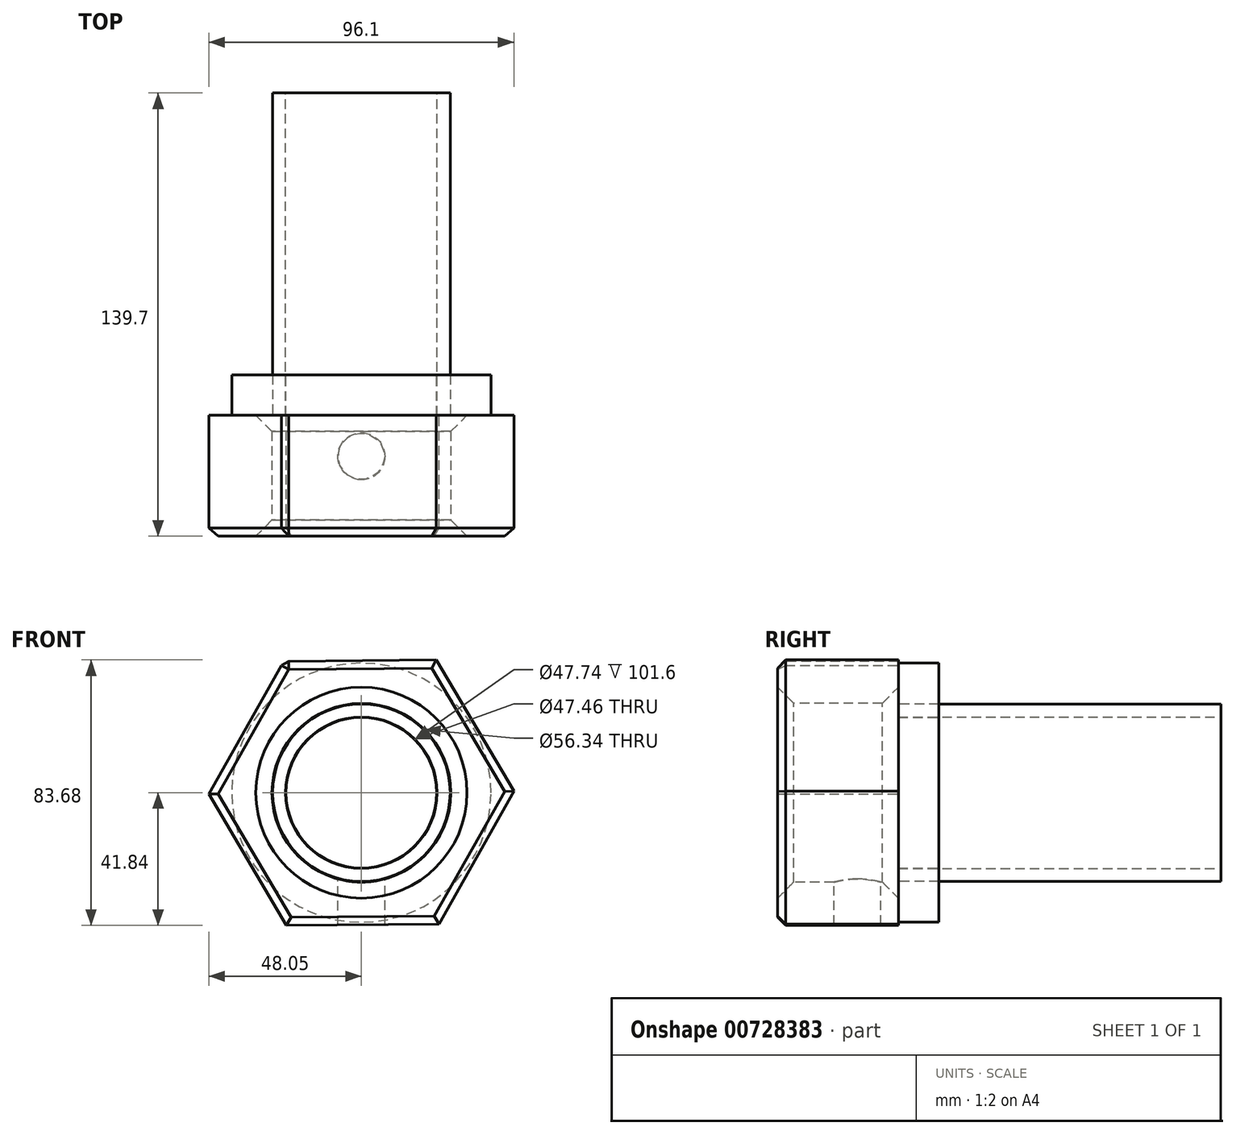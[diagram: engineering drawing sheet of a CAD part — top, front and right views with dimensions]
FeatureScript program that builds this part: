
annotation { "Feature Type Name" : "Feature", "Feature Type Description" : "" }
export const myFeature = defineFeature(function(context is Context, id is Id, definition is map)
    precondition{}
    {
        {
            var Q0;
            Q0=qCreatedBy(makeId("Front.planeOp"),FACE);
            var sketch = newSketch(context, id + "F0", { "sketchPlane" : qUnion([Q0])});
            skCircle(sketch, "E0.cCircle", {"center": v(0, 0) * mm, "radius": 41.62 * mm, "construction": true});
            skLineSegment(sketch, "E0.0", {"start": v(23.64, 41.84) * mm, "end": v(48.05, 0.45) * mm});
            skLineSegment(sketch, "E0.1", {"start": v(48.05, 0.45) * mm, "end": v(24.42, -41.4) * mm});
            skLineSegment(sketch, "E0.2", {"start": v(24.42, -41.4) * mm, "end": v(-23.64, -41.84) * mm});
            skLineSegment(sketch, "E0.3", {"start": v(-23.64, -41.84) * mm, "end": v(-48.05, -0.45) * mm});
            skLineSegment(sketch, "E0.4", {"start": v(-48.05, -0.45) * mm, "end": v(-24.42, 41.4) * mm});
            skLineSegment(sketch, "E0.5", {"start": v(-24.42, 41.4) * mm, "end": v(23.64, 41.84) * mm});
            skPoint(sketch, "E0.0.midPoint", {"position": v(35.85, 21.15) * mm});
            skSolve(sketch);
        }
        {
            var Q0;
            Q0 = qSketchRegion(id + "F0", true);
            extrude(context, id + "F1", {"entities" : qUnion([Q0]), "depth" : 38.1 * mm, "offsetDistance" : 25.4 * mm});
        }
        {
            var Q0;
            Q0=makeQuery(id+"F1.opExtrude","CAP_FACE",FACE,{"disambiguationData":[OSD([sQuery(id+"F0.wireOp",EDGE,"E0.0"),sQuery(id+"F0.wireOp",EDGE,"E0.1"),sQuery(id+"F0.wireOp",EDGE,"E0.2"),sQuery(id+"F0.wireOp",EDGE,"E0.3"),sQuery(id+"F0.wireOp",EDGE,"E0.4"),sQuery(id+"F0.wireOp",EDGE,"E0.5")])],"isStart":false});
            var sketch = newSketch(context, id + "F2", { "sketchPlane" : qUnion([Q0])});
            skCircle(sketch, "E1", {"center": v(0, 0) * mm, "radius": 29.53 * mm});
            skSolve(sketch);
        }
        {
            var Q0;
            Q0=makeQuery(id+"F2.imprint","IMPRINT",FACE,{"disambiguationData":[TD([[makeQuery(id+"F2.imprint","IMPRINT",EDGE,{"derivedFrom":sQuery(id+"F2.wireOp",EDGE,"E1")}),1.0]])]});
            extrude(context, id + "F3", {"entities" : qUnion([Q0]), "operationType" : NewBodyOperationType.REMOVE, "depth" : 38.1 * mm, "offsetDistance" : 25.4 * mm});
        }
        {
            var Q0;
            Q0=makeQuery(id+"F1.opExtrude","CAP_FACE",FACE,{"disambiguationData":[OSD([sQuery(id+"F0.wireOp",EDGE,"E0.0"),sQuery(id+"F0.wireOp",EDGE,"E0.1"),sQuery(id+"F0.wireOp",EDGE,"E0.2"),sQuery(id+"F0.wireOp",EDGE,"E0.3"),sQuery(id+"F0.wireOp",EDGE,"E0.4"),sQuery(id+"F0.wireOp",EDGE,"E0.5")])],"isStart":false});
            var sketch = newSketch(context, id + "F4", { "sketchPlane" : qUnion([Q0])});
            skCircle(sketch, "E2", {"center": v(0, 0) * mm, "radius": 28.17 * mm});
            skSolve(sketch);
        }
        {
            var Q0;
            Q0 = qSketchRegion(id + "F4", true);
            extrude(context, id + "F5", {"entities" : qUnion([Q0]), "operationType" : NewBodyOperationType.REMOVE, "oppositeDirection" : true, "depth" : 38.1 * mm, "offsetDistance" : 25.4 * mm});
        }
        {
            var Q0;
            Q0=makeQuery(id+"F1.opExtrude","CAP_FACE",FACE,{"disambiguationData":[OSD([sQuery(id+"F0.wireOp",EDGE,"E0.0"),sQuery(id+"F0.wireOp",EDGE,"E0.1"),sQuery(id+"F0.wireOp",EDGE,"E0.2"),sQuery(id+"F0.wireOp",EDGE,"E0.3"),sQuery(id+"F0.wireOp",EDGE,"E0.4"),sQuery(id+"F0.wireOp",EDGE,"E0.5")])],"isStart":false});
            var sketch = newSketch(context, id + "F6", { "sketchPlane" : qUnion([Q0])});
            skSolve(sketch);
        }
        {
            var Q0;
            Q0=makeQuery(id+"F1.opExtrude","CAP_EDGE",EDGE,{"disambiguationData":[OSD([sQuery(id+"F0.wireOp",EDGE,"E0.3")])],"isStart":false});
            chamfer(context, id + "F7", {"entities" : qUnion([Q0]), "width" : 2.54 * mm, "tangentPropagation" : true});
        }
        {
            var Q0;
            Q0=makeQuery(id+"F1.opExtrude","CAP_EDGE",EDGE,{"disambiguationData":[OSD([sQuery(id+"F0.wireOp",EDGE,"E0.5")])],"isStart":false});
            var Q1;
            Q1=makeQuery(id+"F1.opExtrude","CAP_EDGE",EDGE,{"disambiguationData":[OSD([sQuery(id+"F0.wireOp",EDGE,"E0.0")])],"isStart":false});
            var Q2;
            Q2=makeQuery(id+"F1.opExtrude","CAP_EDGE",EDGE,{"disambiguationData":[OSD([sQuery(id+"F0.wireOp",EDGE,"E0.1")])],"isStart":false});
            var Q3;
            Q3=makeQuery(id+"F1.opExtrude","CAP_EDGE",EDGE,{"disambiguationData":[OSD([sQuery(id+"F0.wireOp",EDGE,"E0.2")])],"isStart":false});
            var Q4;
            Q4=makeQuery(id+"F1.opExtrude","CAP_EDGE",EDGE,{"disambiguationData":[OSD([sQuery(id+"F0.wireOp",EDGE,"E0.4")])],"isStart":false});
            var Q5;
            Q5=makeQuery(id+"F1.opExtrude","SWEPT_EDGE",EDGE,{"disambiguationData":[OSD([sQuery(id+"F0.wireOp",EDGE,"E0.4"),sQuery(id+"F0.wireOp",EDGE,"E0.5")])]});
            chamfer(context, id + "F8", {"entities" : qUnion([Q0, Q1, Q2, Q3, Q4, Q5]), "width" : 2.54 * mm, "tangentPropagation" : true});
        }
        {
            var Q0;
            Q0=makeQuery(id+"F5.boolean.opBoolean","COPY",FACE,{"derivedFrom":makeQuery(id+"F5.opExtrude","SWEPT_FACE",FACE,{"disambiguationData":[OSD([sQuery(id+"F4.wireOp",EDGE,"E2")])]})});
            chamfer(context, id + "F9", {"entities" : qUnion([Q0]), "width" : 5.08 * mm, "tangentPropagation" : true});
        }
        {
            var Q0;
            Q0=qCreatedBy(makeId("Front.planeOp"),FACE);
            var sketch = newSketch(context, id + "F10", { "sketchPlane" : qUnion([Q0])});
            skCircle(sketch, "E3", {"center": v(0, 0) * mm, "radius": 27.97 * mm});
            skSolve(sketch);
        }
        {
            var Q0;
            Q0 = qSketchRegion(id + "F10", true);
            extrude(context, id + "F11", {"entities" : qUnion([Q0]), "oppositeDirection" : true, "depth" : 101.6 * mm, "offsetDistance" : 25.4 * mm});
        }
        {
            var Q0;
            Q0=qCreatedBy(makeId("Top.planeOp"),FACE);
            var sketch = newSketch(context, id + "F12", { "sketchPlane" : qUnion([Q0])});
            skCircle(sketch, "E4", {"center": v(0, -12.9) * mm, "radius": 7.4 * mm});
            skSolve(sketch);
        }
        {
            var Q0;
            Q0 = qSketchRegion(id + "F12", true);
            extrude(context, id + "F13", {"entities" : qUnion([Q0]), "operationType" : NewBodyOperationType.REMOVE, "oppositeDirection" : true, "depth" : 50.8 * mm, "offsetDistance" : 25.4 * mm});
        }
        {
            var Q0;
            Q0=makeQuery(id+"F11.opExtrude","CAP_FACE",FACE,{"disambiguationData":[OSD([sQuery(id+"F10.wireOp",EDGE,"E3")])],"isStart":false});
            var Q1;
            Q1=makeQuery(id+"F11.opExtrude","SWEPT_BODY",BODY,{"disambiguationData":[OSD([sQuery(id+"F10.wireOp",EDGE,"E3")])]});
            shell(context, id + "F14", {"isHollow" : true, "entities" : qUnion([Q0]), "parts" : qUnion([Q1]), "thickness" : 12.7 * mm});
        }
        {
            var Q0;
            Q0=makeQuery(id+"F11.opExtrude","CAP_FACE",FACE,{"disambiguationData":[OSD([sQuery(id+"F10.wireOp",EDGE,"E3")])],"isStart":false});
            var sketch = newSketch(context, id + "F15", { "sketchPlane" : qUnion([Q0])});
            skCircle(sketch, "E5", {"center": v(0, 0) * mm, "radius": 23.87 * mm});
            skSolve(sketch);
        }
        {
            var Q0;
            Q0 = qSketchRegion(id + "F15", true);
            extrude(context, id + "F16", {"entities" : qUnion([Q0]), "operationType" : NewBodyOperationType.REMOVE, "oppositeDirection" : true, "depth" : 101.6 * mm, "offsetDistance" : 25.4 * mm});
        }
        {
            var Q0;
            Q0=qCreatedBy(makeId("Front.planeOp"),FACE);
            var sketch = newSketch(context, id + "F17", { "sketchPlane" : qUnion([Q0])});
            skCircle(sketch, "E6", {"center": v(0, 0) * mm, "radius": 40.83 * mm});
            skSolve(sketch);
        }
        {
            var Q0;
            Q0 = qSketchRegion(id + "F17", true);
            extrude(context, id + "F18", {"entities" : qUnion([Q0]), "oppositeDirection" : true, "depth" : 12.7 * mm, "offsetDistance" : 25.4 * mm});
        }
        {
            var Q0;
            Q0=makeQuery(id+"F18.opExtrude","CAP_FACE",FACE,{"disambiguationData":[OSD([sQuery(id+"F17.wireOp",EDGE,"E6")])],"isStart":false});
            var sketch = newSketch(context, id + "F19", { "sketchPlane" : qUnion([Q0])});
            skCircle(sketch, "E7", {"center": v(0, 0) * mm, "radius": 23.73 * mm});
            skSolve(sketch);
        }
        {
            var Q0;
            Q0 = qSketchRegion(id + "F19", true);
            extrude(context, id + "F20", {"entities" : qUnion([Q0]), "operationType" : NewBodyOperationType.REMOVE, "oppositeDirection" : true, "depth" : 25.4 * mm, "offsetDistance" : 25.4 * mm});
        }
    });
